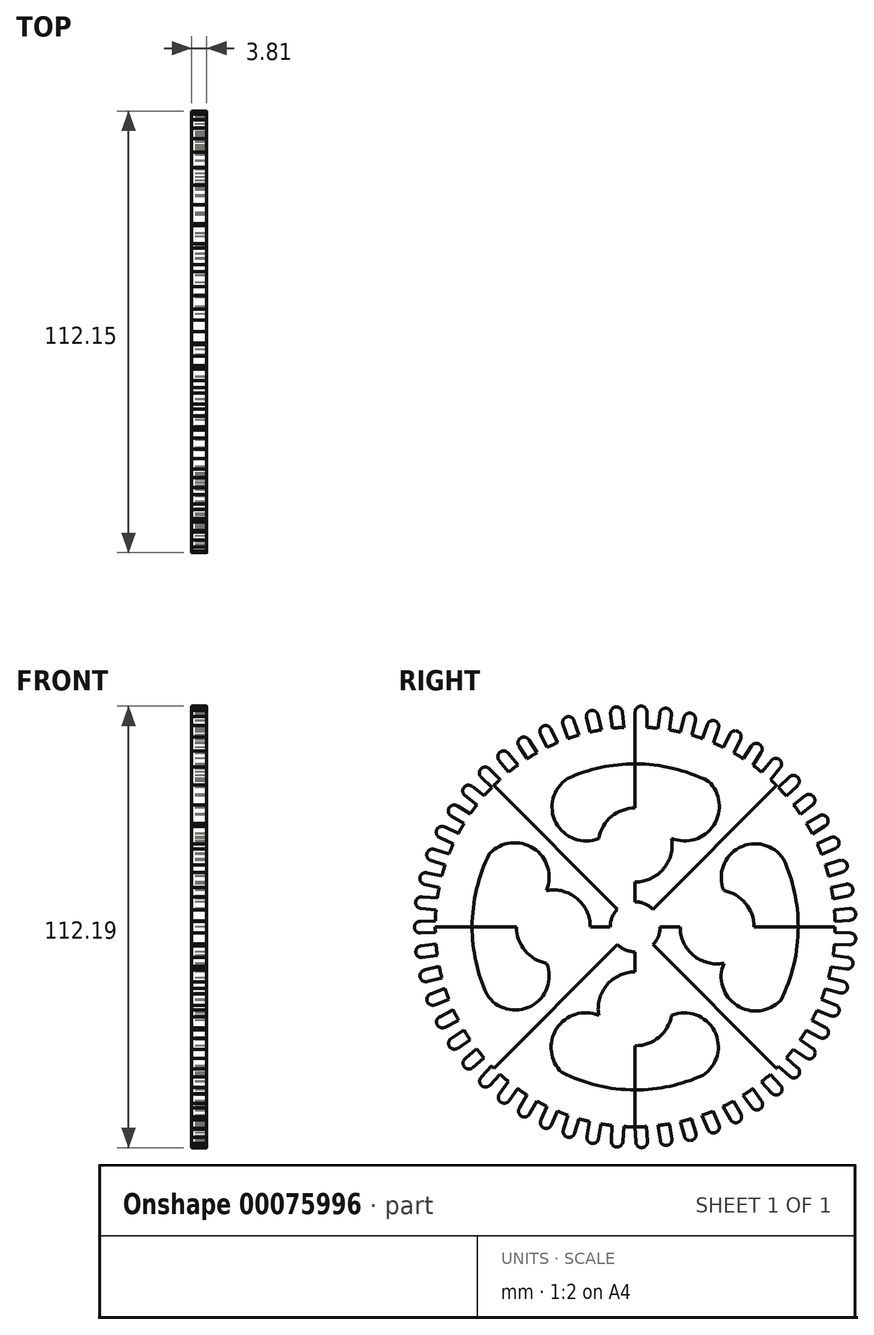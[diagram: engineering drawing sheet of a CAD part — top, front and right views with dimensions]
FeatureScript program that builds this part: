
annotation { "Feature Type Name" : "Feature", "Feature Type Description" : "" }
export const myFeature = defineFeature(function(context is Context, id is Id, definition is map)
    precondition{}
    {
        {
            var Q0;
            Q0=qCreatedBy(makeId("Right.planeOp"),FACE);
            var sketch = newSketch(context, id + "F0", { "sketchPlane" : qUnion([Q0])});
            skCircle(sketch, "E0", {"center": v(-2.48, 1.96) * mm, "radius": 50.8 * mm});
            skCircle(sketch, "E1", {"center": v(-2.48, 1.96) * mm, "radius": 6.35 * mm});
            skLineSegment(sketch, "E2", {"start": v(-2.48, 1.96) * mm, "end": v(-2.48, -48.84) * mm});
            skLineSegment(sketch, "E3.1.0", {"start": v(-2.48, 1.96) * mm, "end": v(33.44, -33.96) * mm});
            skLineSegment(sketch, "E3.2.0", {"start": v(-2.48, 1.96) * mm, "end": v(48.32, 1.96) * mm});
            skLineSegment(sketch, "E3.3.0", {"start": v(-2.48, 1.96) * mm, "end": v(33.44, 37.88) * mm});
            skLineSegment(sketch, "E3.4.0", {"start": v(-2.48, 1.96) * mm, "end": v(-2.48, 52.76) * mm});
            skLineSegment(sketch, "E3.5.0", {"start": v(-2.48, 1.96) * mm, "end": v(-38.4, 37.88) * mm});
            skLineSegment(sketch, "E3.6.0", {"start": v(-2.48, 1.96) * mm, "end": v(-53.28, 1.96) * mm});
            skLineSegment(sketch, "E3.7.0", {"start": v(-2.48, 1.96) * mm, "end": v(-38.4, -33.96) * mm});
            skCircle(sketch, "E4", {"center": v(-23.3, 1.96) * mm, "radius": 9.4 * mm});
            skCircle(sketch, "E5.1.0", {"center": v(-2.48, -18.85) * mm, "radius": 9.4 * mm});
            skCircle(sketch, "E5.2.0", {"center": v(18.34, 1.96) * mm, "radius": 9.4 * mm});
            skCircle(sketch, "E5.3.0", {"center": v(-2.48, 22.78) * mm, "radius": 9.4 * mm});
            skPoint(sketch, "E6", {"position": v(-11.72, 24.46) * mm});
            skPoint(sketch, "E7", {"position": v(6.76, 24.46) * mm});
            skPoint(sketch, "E8", {"position": v(20.02, 11.2) * mm});
            skPoint(sketch, "E9", {"position": v(20.02, -7.28) * mm});
            skPoint(sketch, "E10", {"position": v(6.76, -20.54) * mm});
            skPoint(sketch, "E11", {"position": v(-11.72, -20.54) * mm});
            skPoint(sketch, "E12", {"position": v(-24.97, -7.28) * mm});
            skPoint(sketch, "E13", {"position": v(-24.97, 11.2) * mm});
            skArc(sketch, "E14", {"start": v(-24.97, 11.2) * mm, "mid": v(-26.8, 1.96) * mm, "end": v(-24.97, -7.28) * mm});
            skArc(sketch, "E15.1.0", {"start": v(-11.72, -20.53) * mm, "mid": v(-2.48, -22.36) * mm, "end": v(6.77, -20.53) * mm});
            skArc(sketch, "E15.2.0", {"start": v(20.02, -7.28) * mm, "mid": v(21.84, 1.96) * mm, "end": v(20.02, 11.2) * mm});
            skArc(sketch, "E15.3.0", {"start": v(6.77, 24.45) * mm, "mid": v(-2.48, 26.28) * mm, "end": v(-11.72, 24.45) * mm});
            skArc(sketch, "E16", {"start": v(-11.72, -20.53) * mm, "mid": v(-22.43, -23.88) * mm, "end": v(-21.12, -35.03) * mm});
            skArc(sketch, "E17.1.0", {"start": v(20.02, -7.28) * mm, "mid": v(23.36, -18) * mm, "end": v(34.51, -16.68) * mm});
            skArc(sketch, "E17.2.0", {"start": v(6.77, 24.45) * mm, "mid": v(17.48, 27.8) * mm, "end": v(16.17, 38.95) * mm});
            skArc(sketch, "E17.3.0", {"start": v(-24.97, 11.2) * mm, "mid": v(-28.32, 21.92) * mm, "end": v(-39.47, 20.6) * mm});
            skArc(sketch, "E18", {"start": v(6.77, -20.53) * mm, "mid": v(17.66, -24.5) * mm, "end": v(14.73, -35.72) * mm});
            skArc(sketch, "E19.1.0", {"start": v(20.02, 11.2) * mm, "mid": v(23.98, 22.1) * mm, "end": v(35.2, 19.16) * mm});
            skArc(sketch, "E19.2.0", {"start": v(-11.72, 24.45) * mm, "mid": v(-22.62, 28.42) * mm, "end": v(-19.68, 39.64) * mm});
            skArc(sketch, "E19.3.0", {"start": v(-24.97, -7.28) * mm, "mid": v(-28.94, -18.18) * mm, "end": v(-40.16, -15.24) * mm});
            skArc(sketch, "E20", {"start": v(14.73, -35.72) * mm, "mid": v(-3.28, -39.45) * mm, "end": v(-21.12, -35.03) * mm});
            skArc(sketch, "E21.1.0", {"start": v(35.2, 19.16) * mm, "mid": v(38.94, 1.16) * mm, "end": v(34.51, -16.68) * mm});
            skArc(sketch, "E21.2.0", {"start": v(-19.68, 39.64) * mm, "mid": v(-1.68, 43.38) * mm, "end": v(16.17, 38.95) * mm});
            skArc(sketch, "E21.3.0", {"start": v(-40.16, -15.24) * mm, "mid": v(-43.9, 2.76) * mm, "end": v(-39.47, 20.6) * mm});
            skLineSegment(sketch, "E22", {"start": v(-2.48, 52.76) * mm, "end": v(-2.48, 56.57) * mm});
            skLineSegment(sketch, "E23", {"start": v(0.5, 52.67) * mm, "end": v(0.5, 56.48) * mm});
            skArc(sketch, "E24", {"start": v(0.5, 56.48) * mm, "mid": v(-0.95, 58.06) * mm, "end": v(-2.48, 56.57) * mm});
            skLineSegment(sketch, "E25.1.0", {"start": v(-8.27, 52.43) * mm, "end": v(-8.7, 56.21) * mm});
            skArc(sketch, "E25.1.1", {"start": v(-5.74, 56.47) * mm, "mid": v(-7.35, 57.87) * mm, "end": v(-8.7, 56.21) * mm});
            skLineSegment(sketch, "E25.1.2", {"start": v(-5.3, 52.68) * mm, "end": v(-5.74, 56.47) * mm});
            skLineSegment(sketch, "E25.2.0", {"start": v(-13.98, 51.44) * mm, "end": v(-14.85, 55.15) * mm});
            skArc(sketch, "E25.2.1", {"start": v(-11.93, 55.74) * mm, "mid": v(-13.7, 56.95) * mm, "end": v(-14.85, 55.15) * mm});
            skLineSegment(sketch, "E25.2.2", {"start": v(-11.07, 52.03) * mm, "end": v(-11.93, 55.74) * mm});
            skLineSegment(sketch, "E25.3.0", {"start": v(-19.55, 49.8) * mm, "end": v(-20.83, 53.4) * mm});
            skArc(sketch, "E25.3.1", {"start": v(-18, 54.31) * mm, "mid": v(-19.89, 55.3) * mm, "end": v(-20.83, 53.4) * mm});
            skLineSegment(sketch, "E25.3.2", {"start": v(-16.72, 50.72) * mm, "end": v(-18, 54.31) * mm});
            skLineSegment(sketch, "E25.4.0", {"start": v(-24.9, 47.55) * mm, "end": v(-26.57, 50.97) * mm});
            skArc(sketch, "E25.4.1", {"start": v(-23.87, 52.2) * mm, "mid": v(-25.85, 52.98) * mm, "end": v(-26.57, 50.97) * mm});
            skLineSegment(sketch, "E25.4.2", {"start": v(-22.19, 48.78) * mm, "end": v(-23.87, 52.2) * mm});
            skLineSegment(sketch, "E25.5.0", {"start": v(-29.94, 44.7) * mm, "end": v(-32, 47.9) * mm});
            skArc(sketch, "E25.5.1", {"start": v(-29.45, 49.44) * mm, "mid": v(-31.52, 49.98) * mm, "end": v(-32, 47.9) * mm});
            skLineSegment(sketch, "E25.5.2", {"start": v(-27.4, 46.23) * mm, "end": v(-29.45, 49.44) * mm});
            skLineSegment(sketch, "E25.6.0", {"start": v(-34.63, 41.29) * mm, "end": v(-37.05, 44.24) * mm});
            skArc(sketch, "E25.6.1", {"start": v(-34.7, 46.05) * mm, "mid": v(-36.8, 46.36) * mm, "end": v(-37.05, 44.24) * mm});
            skLineSegment(sketch, "E25.6.2", {"start": v(-32.28, 43.1) * mm, "end": v(-34.7, 46.05) * mm});
            skLineSegment(sketch, "E25.7.0", {"start": v(-38.9, 37.37) * mm, "end": v(-41.64, 40.02) * mm});
            skArc(sketch, "E25.7.1", {"start": v(-39.5, 42.1) * mm, "mid": v(-41.64, 42.15) * mm, "end": v(-41.64, 40.02) * mm});
            skLineSegment(sketch, "E25.7.2", {"start": v(-36.77, 39.44) * mm, "end": v(-39.5, 42.1) * mm});
            skLineSegment(sketch, "E25.8.0", {"start": v(-42.7, 32.98) * mm, "end": v(-45.72, 35.3) * mm});
            skArc(sketch, "E25.8.1", {"start": v(-43.84, 37.6) * mm, "mid": v(-45.97, 37.43) * mm, "end": v(-45.72, 35.3) * mm});
            skLineSegment(sketch, "E25.8.2", {"start": v(-40.82, 35.28) * mm, "end": v(-43.84, 37.6) * mm});
            skLineSegment(sketch, "E25.9.0", {"start": v(-45.98, 28.2) * mm, "end": v(-49.24, 30.16) * mm});
            skArc(sketch, "E25.9.1", {"start": v(-47.63, 32.66) * mm, "mid": v(-49.72, 32.24) * mm, "end": v(-49.24, 30.16) * mm});
            skLineSegment(sketch, "E25.9.2", {"start": v(-44.37, 30.7) * mm, "end": v(-47.63, 32.66) * mm});
            skLineSegment(sketch, "E25.10.0", {"start": v(-48.69, 23.06) * mm, "end": v(-52.15, 24.65) * mm});
            skArc(sketch, "E25.10.1", {"start": v(-50.84, 27.31) * mm, "mid": v(-52.87, 26.66) * mm, "end": v(-52.15, 24.65) * mm});
            skLineSegment(sketch, "E25.10.2", {"start": v(-47.37, 25.73) * mm, "end": v(-50.84, 27.31) * mm});
            skLineSegment(sketch, "E25.11.0", {"start": v(-50.8, 17.66) * mm, "end": v(-54.41, 18.84) * mm});
            skArc(sketch, "E25.11.1", {"start": v(-53.41, 21.64) * mm, "mid": v(-55.35, 20.75) * mm, "end": v(-54.41, 18.84) * mm});
            skLineSegment(sketch, "E25.11.2", {"start": v(-49.79, 20.46) * mm, "end": v(-53.41, 21.64) * mm});
            skLineSegment(sketch, "E25.12.0", {"start": v(-52.27, 12.05) * mm, "end": v(-56, 12.8) * mm});
            skArc(sketch, "E25.12.1", {"start": v(-55.32, 15.7) * mm, "mid": v(-57.15, 14.6) * mm, "end": v(-56, 12.8) * mm});
            skLineSegment(sketch, "E25.12.2", {"start": v(-51.59, 14.94) * mm, "end": v(-55.32, 15.7) * mm});
            skLineSegment(sketch, "E25.13.0", {"start": v(-53.1, 6.3) * mm, "end": v(-56.89, 6.63) * mm});
            skArc(sketch, "E25.13.1", {"start": v(-56.55, 9.59) * mm, "mid": v(-58.24, 8.29) * mm, "end": v(-56.89, 6.63) * mm});
            skLineSegment(sketch, "E25.13.2", {"start": v(-52.75, 9.26) * mm, "end": v(-56.55, 9.59) * mm});
            skLineSegment(sketch, "E25.14.0", {"start": v(-53.26, 0.51) * mm, "end": v(-57.06, 0.4) * mm});
            skArc(sketch, "E25.14.1", {"start": v(-57.06, 3.37) * mm, "mid": v(-58.6, 1.89) * mm, "end": v(-57.06, 0.4) * mm});
            skLineSegment(sketch, "E25.14.2", {"start": v(-53.25, 3.48) * mm, "end": v(-57.06, 3.37) * mm});
            skLineSegment(sketch, "E25.15.0", {"start": v(-52.76, -5.27) * mm, "end": v(-56.53, -5.81) * mm});
            skArc(sketch, "E25.15.1", {"start": v(-56.87, -2.86) * mm, "mid": v(-58.22, -4.5) * mm, "end": v(-56.53, -5.81) * mm});
            skLineSegment(sketch, "E25.15.2", {"start": v(-53.1, -2.31) * mm, "end": v(-56.87, -2.86) * mm});
            skLineSegment(sketch, "E25.16.0", {"start": v(-51.6, -10.95) * mm, "end": v(-55.3, -11.92) * mm});
            skArc(sketch, "E25.16.1", {"start": v(-55.96, -9.03) * mm, "mid": v(-57.12, -10.82) * mm, "end": v(-55.3, -11.92) * mm});
            skLineSegment(sketch, "E25.16.2", {"start": v(-52.28, -8.06) * mm, "end": v(-55.96, -9.03) * mm});
            skLineSegment(sketch, "E25.17.0", {"start": v(-49.82, -16.47) * mm, "end": v(-53.37, -17.85) * mm});
            skArc(sketch, "E25.17.1", {"start": v(-54.36, -15.05) * mm, "mid": v(-55.3, -16.96) * mm, "end": v(-53.37, -17.85) * mm});
            skLineSegment(sketch, "E25.17.2", {"start": v(-50.81, -13.67) * mm, "end": v(-54.36, -15.05) * mm});
            skLineSegment(sketch, "E25.18.0", {"start": v(-47.4, -21.75) * mm, "end": v(-50.78, -23.52) * mm});
            skArc(sketch, "E25.18.1", {"start": v(-52.09, -20.85) * mm, "mid": v(-52.8, -22.86) * mm, "end": v(-50.78, -23.52) * mm});
            skLineSegment(sketch, "E25.18.2", {"start": v(-48.72, -19.08) * mm, "end": v(-52.09, -20.85) * mm});
            skLineSegment(sketch, "E25.19.0", {"start": v(-44.41, -26.71) * mm, "end": v(-47.56, -28.86) * mm});
            skArc(sketch, "E25.19.1", {"start": v(-49.16, -26.36) * mm, "mid": v(-49.65, -28.44) * mm, "end": v(-47.56, -28.86) * mm});
            skLineSegment(sketch, "E25.19.2", {"start": v(-46.02, -24.21) * mm, "end": v(-49.16, -26.36) * mm});
            skLineSegment(sketch, "E25.20.0", {"start": v(-40.87, -31.3) * mm, "end": v(-43.75, -33.8) * mm});
            skArc(sketch, "E25.20.1", {"start": v(-45.63, -31.5) * mm, "mid": v(-45.87, -33.62) * mm, "end": v(-43.75, -33.8) * mm});
            skLineSegment(sketch, "E25.20.2", {"start": v(-42.75, -29) * mm, "end": v(-45.63, -31.5) * mm});
            skLineSegment(sketch, "E25.21.0", {"start": v(-36.83, -35.47) * mm, "end": v(-39.4, -38.27) * mm});
            skArc(sketch, "E25.21.1", {"start": v(-41.53, -36.2) * mm, "mid": v(-41.54, -38.33) * mm, "end": v(-39.4, -38.27) * mm});
            skLineSegment(sketch, "E25.21.2", {"start": v(-38.96, -33.4) * mm, "end": v(-41.53, -36.2) * mm});
            skLineSegment(sketch, "E25.22.0", {"start": v(-32.34, -39.14) * mm, "end": v(-34.58, -42.22) * mm});
            skArc(sketch, "E25.22.1", {"start": v(-36.93, -40.4) * mm, "mid": v(-36.69, -42.52) * mm, "end": v(-34.58, -42.22) * mm});
            skLineSegment(sketch, "E25.22.2", {"start": v(-34.69, -37.32) * mm, "end": v(-36.93, -40.4) * mm});
            skLineSegment(sketch, "E25.23.0", {"start": v(-27.46, -42.27) * mm, "end": v(-29.33, -45.6) * mm});
            skArc(sketch, "E25.23.1", {"start": v(-31.88, -44.05) * mm, "mid": v(-31.4, -46.13) * mm, "end": v(-29.33, -45.6) * mm});
            skLineSegment(sketch, "E25.23.2", {"start": v(-30, -40.74) * mm, "end": v(-31.88, -44.05) * mm});
            skLineSegment(sketch, "E25.24.0", {"start": v(-22.25, -44.83) * mm, "end": v(-23.74, -48.34) * mm});
            skArc(sketch, "E25.24.1", {"start": v(-26.44, -47.1) * mm, "mid": v(-25.72, -49.12) * mm, "end": v(-23.74, -48.34) * mm});
            skLineSegment(sketch, "E25.24.2", {"start": v(-24.96, -43.6) * mm, "end": v(-26.44, -47.1) * mm});
            skLineSegment(sketch, "E25.25.0", {"start": v(-16.79, -46.78) * mm, "end": v(-17.86, -50.44) * mm});
            skArc(sketch, "E25.25.1", {"start": v(-20.69, -49.52) * mm, "mid": v(-19.75, -51.43) * mm, "end": v(-17.86, -50.44) * mm});
            skLineSegment(sketch, "E25.25.2", {"start": v(-19.62, -45.86) * mm, "end": v(-20.69, -49.52) * mm});
            skLineSegment(sketch, "E25.26.0", {"start": v(-11.14, -48.1) * mm, "end": v(-11.79, -51.85) * mm});
            skArc(sketch, "E25.26.1", {"start": v(-14.7, -51.26) * mm, "mid": v(-13.55, -53.05) * mm, "end": v(-11.79, -51.85) * mm});
            skLineSegment(sketch, "E25.26.2", {"start": v(-14.05, -47.5) * mm, "end": v(-14.7, -51.26) * mm});
            skLineSegment(sketch, "E25.27.0", {"start": v(-5.38, -48.76) * mm, "end": v(-5.6, -52.56) * mm});
            skArc(sketch, "E25.27.1", {"start": v(-8.56, -52.3) * mm, "mid": v(-7.2, -53.96) * mm, "end": v(-5.6, -52.56) * mm});
            skLineSegment(sketch, "E25.27.2", {"start": v(-8.34, -48.5) * mm, "end": v(-8.56, -52.3) * mm});
            skLineSegment(sketch, "E25.28.0", {"start": v(0.42, -48.76) * mm, "end": v(0.64, -52.56) * mm});
            skArc(sketch, "E25.28.1", {"start": v(-2.33, -52.64) * mm, "mid": v(-0.8, -54.13) * mm, "end": v(0.64, -52.56) * mm});
            skLineSegment(sketch, "E25.28.2", {"start": v(-2.55, -48.84) * mm, "end": v(-2.33, -52.64) * mm});
            skLineSegment(sketch, "E25.29.0", {"start": v(6.19, -48.1) * mm, "end": v(6.84, -51.85) * mm});
            skArc(sketch, "E25.29.1", {"start": v(3.9, -52.27) * mm, "mid": v(5.58, -53.57) * mm, "end": v(6.84, -51.85) * mm});
            skLineSegment(sketch, "E25.29.2", {"start": v(3.24, -48.52) * mm, "end": v(3.9, -52.27) * mm});
            skLineSegment(sketch, "E25.30.0", {"start": v(11.84, -46.78) * mm, "end": v(12.9, -50.44) * mm});
            skArc(sketch, "E25.30.1", {"start": v(10.03, -51.2) * mm, "mid": v(11.86, -52.3) * mm, "end": v(12.9, -50.44) * mm});
            skLineSegment(sketch, "E25.30.2", {"start": v(8.96, -47.54) * mm, "end": v(10.03, -51.2) * mm});
            skLineSegment(sketch, "E25.31.0", {"start": v(17.3, -44.83) * mm, "end": v(18.78, -48.34) * mm});
            skArc(sketch, "E25.31.1", {"start": v(16, -49.42) * mm, "mid": v(17.95, -50.3) * mm, "end": v(18.78, -48.34) * mm});
            skLineSegment(sketch, "E25.31.2", {"start": v(14.53, -45.9) * mm, "end": v(16, -49.42) * mm});
            skLineSegment(sketch, "E25.32.0", {"start": v(22.5, -42.27) * mm, "end": v(24.38, -45.6) * mm});
            skArc(sketch, "E25.32.1", {"start": v(21.75, -46.98) * mm, "mid": v(23.77, -47.64) * mm, "end": v(24.38, -45.6) * mm});
            skLineSegment(sketch, "E25.32.2", {"start": v(19.87, -43.66) * mm, "end": v(21.75, -46.98) * mm});
            skLineSegment(sketch, "E25.33.0", {"start": v(27.38, -39.14) * mm, "end": v(29.62, -42.22) * mm});
            skArc(sketch, "E25.33.1", {"start": v(27.17, -43.9) * mm, "mid": v(29.26, -44.32) * mm, "end": v(29.62, -42.22) * mm});
            skLineSegment(sketch, "E25.33.2", {"start": v(24.93, -40.81) * mm, "end": v(27.17, -43.9) * mm});
            skLineSegment(sketch, "E25.34.0", {"start": v(31.87, -35.47) * mm, "end": v(34.45, -38.27) * mm});
            skArc(sketch, "E25.34.1", {"start": v(32.2, -40.22) * mm, "mid": v(34.33, -40.4) * mm, "end": v(34.45, -38.27) * mm});
            skLineSegment(sketch, "E25.34.2", {"start": v(29.62, -37.41) * mm, "end": v(32.2, -40.22) * mm});
            skLineSegment(sketch, "E25.35.0", {"start": v(35.92, -31.3) * mm, "end": v(38.8, -33.8) * mm});
            skArc(sketch, "E25.35.1", {"start": v(36.78, -35.99) * mm, "mid": v(38.92, -35.93) * mm, "end": v(38.8, -33.8) * mm});
            skLineSegment(sketch, "E25.35.2", {"start": v(33.9, -33.5) * mm, "end": v(36.78, -35.99) * mm});
            skLineSegment(sketch, "E25.36.0", {"start": v(39.46, -26.71) * mm, "end": v(42.6, -28.86) * mm});
            skArc(sketch, "E25.36.1", {"start": v(40.85, -31.27) * mm, "mid": v(42.97, -30.97) * mm, "end": v(42.6, -28.86) * mm});
            skLineSegment(sketch, "E25.36.2", {"start": v(37.7, -29.12) * mm, "end": v(40.85, -31.27) * mm});
            skLineSegment(sketch, "E25.37.0", {"start": v(42.45, -21.75) * mm, "end": v(45.82, -23.52) * mm});
            skArc(sketch, "E25.37.1", {"start": v(44.36, -26.11) * mm, "mid": v(46.42, -25.57) * mm, "end": v(45.82, -23.52) * mm});
            skLineSegment(sketch, "E25.37.2", {"start": v(40.99, -24.33) * mm, "end": v(44.36, -26.11) * mm});
            skLineSegment(sketch, "E25.38.0", {"start": v(44.86, -16.47) * mm, "end": v(48.41, -17.85) * mm});
            skArc(sketch, "E25.38.1", {"start": v(47.25, -20.59) * mm, "mid": v(49.24, -19.82) * mm, "end": v(48.41, -17.85) * mm});
            skLineSegment(sketch, "E25.38.2", {"start": v(43.7, -19.2) * mm, "end": v(47.25, -20.59) * mm});
            skLineSegment(sketch, "E25.39.0", {"start": v(46.65, -10.95) * mm, "end": v(50.34, -11.92) * mm});
            skArc(sketch, "E25.39.1", {"start": v(49.5, -14.77) * mm, "mid": v(51.39, -13.78) * mm, "end": v(50.34, -11.92) * mm});
            skLineSegment(sketch, "E25.39.2", {"start": v(45.81, -13.8) * mm, "end": v(49.5, -14.77) * mm});
            skLineSegment(sketch, "E25.40.0", {"start": v(47.8, -5.27) * mm, "end": v(51.58, -5.81) * mm});
            skArc(sketch, "E25.40.1", {"start": v(51.07, -8.74) * mm, "mid": v(52.83, -7.54) * mm, "end": v(51.58, -5.81) * mm});
            skLineSegment(sketch, "E25.40.2", {"start": v(47.3, -8.2) * mm, "end": v(51.07, -8.74) * mm});
            skLineSegment(sketch, "E25.41.0", {"start": v(48.3, 0.51) * mm, "end": v(52.11, 0.4) * mm});
            skArc(sketch, "E25.41.1", {"start": v(51.94, -2.57) * mm, "mid": v(53.55, -1.17) * mm, "end": v(52.11, 0.4) * mm});
            skLineSegment(sketch, "E25.41.2", {"start": v(48.13, -2.46) * mm, "end": v(51.94, -2.57) * mm});
            skLineSegment(sketch, "E25.42.0", {"start": v(48.14, 6.3) * mm, "end": v(51.93, 6.63) * mm});
            skArc(sketch, "E25.42.1", {"start": v(52.1, 3.67) * mm, "mid": v(53.54, 5.24) * mm, "end": v(51.93, 6.63) * mm});
            skLineSegment(sketch, "E25.42.2", {"start": v(48.3, 3.34) * mm, "end": v(52.1, 3.67) * mm});
            skLineSegment(sketch, "E25.43.0", {"start": v(47.31, 12.05) * mm, "end": v(51.05, 12.8) * mm});
            skArc(sketch, "E25.43.1", {"start": v(51.55, 9.88) * mm, "mid": v(52.8, 11.6) * mm, "end": v(51.05, 12.8) * mm});
            skLineSegment(sketch, "E25.43.2", {"start": v(47.82, 9.12) * mm, "end": v(51.55, 9.88) * mm});
            skLineSegment(sketch, "E25.44.0", {"start": v(45.84, 17.66) * mm, "end": v(49.46, 18.84) * mm});
            skArc(sketch, "E25.44.1", {"start": v(50.3, 15.98) * mm, "mid": v(51.35, 17.84) * mm, "end": v(49.46, 18.84) * mm});
            skLineSegment(sketch, "E25.44.2", {"start": v(46.67, 14.8) * mm, "end": v(50.3, 15.98) * mm});
            skLineSegment(sketch, "E25.45.0", {"start": v(43.73, 23.06) * mm, "end": v(47.2, 24.65) * mm});
            skArc(sketch, "E25.45.1", {"start": v(48.35, 21.9) * mm, "mid": v(49.19, 23.87) * mm, "end": v(47.2, 24.65) * mm});
            skLineSegment(sketch, "E25.45.2", {"start": v(44.89, 20.32) * mm, "end": v(48.35, 21.9) * mm});
            skLineSegment(sketch, "E25.46.0", {"start": v(41.03, 28.2) * mm, "end": v(44.29, 30.16) * mm});
            skArc(sketch, "E25.46.1", {"start": v(45.75, 27.57) * mm, "mid": v(46.35, 29.62) * mm, "end": v(44.29, 30.16) * mm});
            skLineSegment(sketch, "E25.46.2", {"start": v(42.49, 25.6) * mm, "end": v(45.75, 27.57) * mm});
            skLineSegment(sketch, "E25.47.0", {"start": v(37.75, 32.98) * mm, "end": v(40.77, 35.3) * mm});
            skArc(sketch, "E25.47.1", {"start": v(42.51, 32.9) * mm, "mid": v(42.88, 35) * mm, "end": v(40.77, 35.3) * mm});
            skLineSegment(sketch, "E25.47.2", {"start": v(39.5, 30.58) * mm, "end": v(42.51, 32.9) * mm});
            skLineSegment(sketch, "E25.48.0", {"start": v(33.95, 37.37) * mm, "end": v(36.69, 40.02) * mm});
            skArc(sketch, "E25.48.1", {"start": v(38.7, 37.83) * mm, "mid": v(38.82, 39.96) * mm, "end": v(36.69, 40.02) * mm});
            skLineSegment(sketch, "E25.48.2", {"start": v(35.96, 35.17) * mm, "end": v(38.7, 37.83) * mm});
            skLineSegment(sketch, "E25.49.0", {"start": v(29.68, 41.29) * mm, "end": v(32.1, 44.24) * mm});
            skArc(sketch, "E25.49.1", {"start": v(34.34, 42.29) * mm, "mid": v(34.22, 44.42) * mm, "end": v(32.1, 44.24) * mm});
            skLineSegment(sketch, "E25.49.2", {"start": v(31.93, 39.34) * mm, "end": v(34.34, 42.29) * mm});
            skLineSegment(sketch, "E25.50.0", {"start": v(24.99, 44.7) * mm, "end": v(27.05, 47.9) * mm});
            skArc(sketch, "E25.50.1", {"start": v(29.5, 46.22) * mm, "mid": v(29.14, 48.32) * mm, "end": v(27.05, 47.9) * mm});
            skLineSegment(sketch, "E25.50.2", {"start": v(27.44, 43.02) * mm, "end": v(29.5, 46.22) * mm});
            skLineSegment(sketch, "E25.51.0", {"start": v(19.94, 47.55) * mm, "end": v(21.62, 50.97) * mm});
            skArc(sketch, "E25.51.1", {"start": v(24.25, 49.58) * mm, "mid": v(23.65, 51.63) * mm, "end": v(21.62, 50.97) * mm});
            skLineSegment(sketch, "E25.51.2", {"start": v(22.57, 46.16) * mm, "end": v(24.25, 49.58) * mm});
            skLineSegment(sketch, "E25.52.0", {"start": v(14.6, 49.8) * mm, "end": v(15.87, 53.4) * mm});
            skArc(sketch, "E25.52.1", {"start": v(18.64, 52.31) * mm, "mid": v(17.82, 54.28) * mm, "end": v(15.87, 53.4) * mm});
            skLineSegment(sketch, "E25.52.2", {"start": v(17.36, 48.73) * mm, "end": v(18.64, 52.31) * mm});
            skLineSegment(sketch, "E25.53.0", {"start": v(9.03, 51.44) * mm, "end": v(9.9, 55.15) * mm});
            skArc(sketch, "E25.53.1", {"start": v(12.77, 54.4) * mm, "mid": v(11.72, 56.25) * mm, "end": v(9.9, 55.15) * mm});
            skLineSegment(sketch, "E25.53.2", {"start": v(11.9, 50.68) * mm, "end": v(12.77, 54.4) * mm});
            skLineSegment(sketch, "E25.54.0", {"start": v(3.31, 52.43) * mm, "end": v(3.75, 56.21) * mm});
            skArc(sketch, "E25.54.1", {"start": v(6.7, 55.79) * mm, "mid": v(5.44, 57.52) * mm, "end": v(3.75, 56.21) * mm});
            skLineSegment(sketch, "E25.54.2", {"start": v(6.26, 52) * mm, "end": v(6.7, 55.79) * mm});
            skSolve(sketch);
        }
        {
            var Q0;
            {var subQ12=sQuery(id+"F0.wireOp",EDGE,"E17.2.0");Q0=makeQuery(id+"F0.imprint","IMPRINT",FACE,{"disambiguationData":[TD([[makeQuery(id+"F0.imprint","IMPRINT",EDGE,{"derivedFrom":subQ12}),-1.0]])]});}
            var Q1;
            {var subQ17=sQuery(id+"F0.wireOp",EDGE,"E19.1.0");Q1=makeQuery(id+"F0.imprint","IMPRINT",FACE,{"disambiguationData":[TD([[makeQuery(id+"F0.imprint","IMPRINT",EDGE,{"derivedFrom":subQ17}),1.0]])]});}
            var Q2;
            {var subQ12=sQuery(id+"F0.wireOp",EDGE,"E17.1.0");Q2=makeQuery(id+"F0.imprint","IMPRINT",FACE,{"disambiguationData":[TD([[makeQuery(id+"F0.imprint","IMPRINT",EDGE,{"derivedFrom":subQ12}),-1.0]])]});}
            var Q3;
            {var subQ16=sQuery(id+"F0.wireOp",EDGE,"E18");Q3=makeQuery(id+"F0.imprint","IMPRINT",FACE,{"disambiguationData":[TD([[makeQuery(id+"F0.imprint","IMPRINT",EDGE,{"derivedFrom":subQ16}),1.0]])]});}
            var Q4;
            {var subQ22=sQuery(id+"F0.wireOp",EDGE,"E16");Q4=makeQuery(id+"F0.imprint","IMPRINT",FACE,{"disambiguationData":[TD([[makeQuery(id+"F0.imprint","IMPRINT",EDGE,{"derivedFrom":subQ22}),-1.0]])]});}
            var Q5;
            {var subQ10=sQuery(id+"F0.wireOp",EDGE,"E19.3.0");Q5=makeQuery(id+"F0.imprint","IMPRINT",FACE,{"disambiguationData":[TD([[makeQuery(id+"F0.imprint","IMPRINT",EDGE,{"derivedFrom":subQ10}),1.0]])]});}
            var Q6;
            {var subQ13=sQuery(id+"F0.wireOp",EDGE,"E17.3.0");Q6=makeQuery(id+"F0.imprint","IMPRINT",FACE,{"disambiguationData":[TD([[makeQuery(id+"F0.imprint","IMPRINT",EDGE,{"derivedFrom":subQ13}),-1.0]])]});}
            var Q7;
            {var subQ13=sQuery(id+"F0.wireOp",EDGE,"E19.2.0");Q7=makeQuery(id+"F0.imprint","IMPRINT",FACE,{"disambiguationData":[TD([[makeQuery(id+"F0.imprint","IMPRINT",EDGE,{"derivedFrom":subQ13}),1.0]])]});}
            var Q8;
            {var subQ0=sQuery(id+"F0.wireOp",EDGE,"E25.8.0");Q8=makeQuery(id+"F0.imprint","IMPRINT",FACE,{"disambiguationData":[TD([[makeQuery(id+"F0.imprint","IMPRINT",EDGE,{"derivedFrom":subQ0}),-1.0]])]});}
            var Q9;
            {var subQ0=sQuery(id+"F0.wireOp",EDGE,"E25.9.0");Q9=makeQuery(id+"F0.imprint","IMPRINT",FACE,{"disambiguationData":[TD([[makeQuery(id+"F0.imprint","IMPRINT",EDGE,{"derivedFrom":subQ0}),-1.0]])]});}
            var Q10;
            {var subQ0=sQuery(id+"F0.wireOp",EDGE,"E25.10.0");Q10=makeQuery(id+"F0.imprint","IMPRINT",FACE,{"disambiguationData":[TD([[makeQuery(id+"F0.imprint","IMPRINT",EDGE,{"derivedFrom":subQ0}),-1.0]])]});}
            var Q11;
            {var subQ0=sQuery(id+"F0.wireOp",EDGE,"E25.11.0");Q11=makeQuery(id+"F0.imprint","IMPRINT",FACE,{"disambiguationData":[TD([[makeQuery(id+"F0.imprint","IMPRINT",EDGE,{"derivedFrom":subQ0}),-1.0]])]});}
            var Q12;
            {var subQ0=sQuery(id+"F0.wireOp",EDGE,"E25.12.0");Q12=makeQuery(id+"F0.imprint","IMPRINT",FACE,{"disambiguationData":[TD([[makeQuery(id+"F0.imprint","IMPRINT",EDGE,{"derivedFrom":subQ0}),-1.0]])]});}
            var Q13;
            {var subQ0=sQuery(id+"F0.wireOp",EDGE,"E25.13.0");Q13=makeQuery(id+"F0.imprint","IMPRINT",FACE,{"disambiguationData":[TD([[makeQuery(id+"F0.imprint","IMPRINT",EDGE,{"derivedFrom":subQ0}),-1.0]])]});}
            var Q14;
            {var subQ0=sQuery(id+"F0.wireOp",EDGE,"E25.14.0");Q14=makeQuery(id+"F0.imprint","IMPRINT",FACE,{"disambiguationData":[TD([[makeQuery(id+"F0.imprint","IMPRINT",EDGE,{"derivedFrom":subQ0}),-1.0]])]});}
            var Q15;
            {var subQ0=sQuery(id+"F0.wireOp",EDGE,"E25.15.0");Q15=makeQuery(id+"F0.imprint","IMPRINT",FACE,{"disambiguationData":[TD([[makeQuery(id+"F0.imprint","IMPRINT",EDGE,{"derivedFrom":subQ0}),-1.0]])]});}
            var Q16;
            {var subQ0=sQuery(id+"F0.wireOp",EDGE,"E25.16.0");Q16=makeQuery(id+"F0.imprint","IMPRINT",FACE,{"disambiguationData":[TD([[makeQuery(id+"F0.imprint","IMPRINT",EDGE,{"derivedFrom":subQ0}),-1.0]])]});}
            var Q17;
            {var subQ0=sQuery(id+"F0.wireOp",EDGE,"E25.17.0");Q17=makeQuery(id+"F0.imprint","IMPRINT",FACE,{"disambiguationData":[TD([[makeQuery(id+"F0.imprint","IMPRINT",EDGE,{"derivedFrom":subQ0}),-1.0]])]});}
            var Q18;
            {var subQ0=sQuery(id+"F0.wireOp",EDGE,"E25.18.0");Q18=makeQuery(id+"F0.imprint","IMPRINT",FACE,{"disambiguationData":[TD([[makeQuery(id+"F0.imprint","IMPRINT",EDGE,{"derivedFrom":subQ0}),-1.0]])]});}
            var Q19;
            {var subQ0=sQuery(id+"F0.wireOp",EDGE,"E25.19.0");Q19=makeQuery(id+"F0.imprint","IMPRINT",FACE,{"disambiguationData":[TD([[makeQuery(id+"F0.imprint","IMPRINT",EDGE,{"derivedFrom":subQ0}),-1.0]])]});}
            var Q20;
            {var subQ0=sQuery(id+"F0.wireOp",EDGE,"E25.20.0");Q20=makeQuery(id+"F0.imprint","IMPRINT",FACE,{"disambiguationData":[TD([[makeQuery(id+"F0.imprint","IMPRINT",EDGE,{"derivedFrom":subQ0}),-1.0]])]});}
            var Q21;
            {var subQ0=sQuery(id+"F0.wireOp",EDGE,"E25.21.0");Q21=makeQuery(id+"F0.imprint","IMPRINT",FACE,{"disambiguationData":[TD([[makeQuery(id+"F0.imprint","IMPRINT",EDGE,{"derivedFrom":subQ0}),-1.0]])]});}
            var Q22;
            {var subQ0=sQuery(id+"F0.wireOp",EDGE,"E25.22.0");Q22=makeQuery(id+"F0.imprint","IMPRINT",FACE,{"disambiguationData":[TD([[makeQuery(id+"F0.imprint","IMPRINT",EDGE,{"derivedFrom":subQ0}),-1.0]])]});}
            var Q23;
            {var subQ0=sQuery(id+"F0.wireOp",EDGE,"E25.23.0");Q23=makeQuery(id+"F0.imprint","IMPRINT",FACE,{"disambiguationData":[TD([[makeQuery(id+"F0.imprint","IMPRINT",EDGE,{"derivedFrom":subQ0}),-1.0]])]});}
            var Q24;
            {var subQ0=sQuery(id+"F0.wireOp",EDGE,"E25.24.0");Q24=makeQuery(id+"F0.imprint","IMPRINT",FACE,{"disambiguationData":[TD([[makeQuery(id+"F0.imprint","IMPRINT",EDGE,{"derivedFrom":subQ0}),-1.0]])]});}
            var Q25;
            {var subQ0=sQuery(id+"F0.wireOp",EDGE,"E25.25.0");Q25=makeQuery(id+"F0.imprint","IMPRINT",FACE,{"disambiguationData":[TD([[makeQuery(id+"F0.imprint","IMPRINT",EDGE,{"derivedFrom":subQ0}),-1.0]])]});}
            var Q26;
            {var subQ0=sQuery(id+"F0.wireOp",EDGE,"E25.26.0");Q26=makeQuery(id+"F0.imprint","IMPRINT",FACE,{"disambiguationData":[TD([[makeQuery(id+"F0.imprint","IMPRINT",EDGE,{"derivedFrom":subQ0}),-1.0]])]});}
            var Q27;
            {var subQ0=sQuery(id+"F0.wireOp",EDGE,"E25.27.0");Q27=makeQuery(id+"F0.imprint","IMPRINT",FACE,{"disambiguationData":[TD([[makeQuery(id+"F0.imprint","IMPRINT",EDGE,{"derivedFrom":subQ0}),-1.0]])]});}
            var Q28;
            {var subQ2=sQuery(id+"F0.wireOp",EDGE,"E25.28.0");Q28=makeQuery(id+"F0.imprint","IMPRINT",FACE,{"disambiguationData":[TD([[makeQuery(id+"F0.imprint","IMPRINT",EDGE,{"derivedFrom":subQ2}),-1.0]])]});}
            var Q29;
            {var subQ0=sQuery(id+"F0.wireOp",EDGE,"E25.29.0");Q29=makeQuery(id+"F0.imprint","IMPRINT",FACE,{"disambiguationData":[TD([[makeQuery(id+"F0.imprint","IMPRINT",EDGE,{"derivedFrom":subQ0}),-1.0]])]});}
            var Q30;
            {var subQ0=sQuery(id+"F0.wireOp",EDGE,"E25.30.0");Q30=makeQuery(id+"F0.imprint","IMPRINT",FACE,{"disambiguationData":[TD([[makeQuery(id+"F0.imprint","IMPRINT",EDGE,{"derivedFrom":subQ0}),-1.0]])]});}
            var Q31;
            {var subQ0=sQuery(id+"F0.wireOp",EDGE,"E25.31.0");Q31=makeQuery(id+"F0.imprint","IMPRINT",FACE,{"disambiguationData":[TD([[makeQuery(id+"F0.imprint","IMPRINT",EDGE,{"derivedFrom":subQ0}),-1.0]])]});}
            var Q32;
            {var subQ0=sQuery(id+"F0.wireOp",EDGE,"E25.32.0");Q32=makeQuery(id+"F0.imprint","IMPRINT",FACE,{"disambiguationData":[TD([[makeQuery(id+"F0.imprint","IMPRINT",EDGE,{"derivedFrom":subQ0}),-1.0]])]});}
            var Q33;
            {var subQ0=sQuery(id+"F0.wireOp",EDGE,"E25.33.0");Q33=makeQuery(id+"F0.imprint","IMPRINT",FACE,{"disambiguationData":[TD([[makeQuery(id+"F0.imprint","IMPRINT",EDGE,{"derivedFrom":subQ0}),-1.0]])]});}
            var Q34;
            {var subQ0=sQuery(id+"F0.wireOp",EDGE,"E25.34.0");Q34=makeQuery(id+"F0.imprint","IMPRINT",FACE,{"disambiguationData":[TD([[makeQuery(id+"F0.imprint","IMPRINT",EDGE,{"derivedFrom":subQ0}),-1.0]])]});}
            var Q35;
            {var subQ0=sQuery(id+"F0.wireOp",EDGE,"E25.35.0");Q35=makeQuery(id+"F0.imprint","IMPRINT",FACE,{"disambiguationData":[TD([[makeQuery(id+"F0.imprint","IMPRINT",EDGE,{"derivedFrom":subQ0}),-1.0]])]});}
            var Q36;
            {var subQ0=sQuery(id+"F0.wireOp",EDGE,"E25.36.0");Q36=makeQuery(id+"F0.imprint","IMPRINT",FACE,{"disambiguationData":[TD([[makeQuery(id+"F0.imprint","IMPRINT",EDGE,{"derivedFrom":subQ0}),-1.0]])]});}
            var Q37;
            {var subQ0=sQuery(id+"F0.wireOp",EDGE,"E25.37.0");Q37=makeQuery(id+"F0.imprint","IMPRINT",FACE,{"disambiguationData":[TD([[makeQuery(id+"F0.imprint","IMPRINT",EDGE,{"derivedFrom":subQ0}),-1.0]])]});}
            var Q38;
            {var subQ0=sQuery(id+"F0.wireOp",EDGE,"E25.38.0");Q38=makeQuery(id+"F0.imprint","IMPRINT",FACE,{"disambiguationData":[TD([[makeQuery(id+"F0.imprint","IMPRINT",EDGE,{"derivedFrom":subQ0}),-1.0]])]});}
            var Q39;
            {var subQ0=sQuery(id+"F0.wireOp",EDGE,"E25.39.0");Q39=makeQuery(id+"F0.imprint","IMPRINT",FACE,{"disambiguationData":[TD([[makeQuery(id+"F0.imprint","IMPRINT",EDGE,{"derivedFrom":subQ0}),-1.0]])]});}
            var Q40;
            {var subQ0=sQuery(id+"F0.wireOp",EDGE,"E25.40.0");Q40=makeQuery(id+"F0.imprint","IMPRINT",FACE,{"disambiguationData":[TD([[makeQuery(id+"F0.imprint","IMPRINT",EDGE,{"derivedFrom":subQ0}),-1.0]])]});}
            var Q41;
            {var subQ0=sQuery(id+"F0.wireOp",EDGE,"E25.41.0");Q41=makeQuery(id+"F0.imprint","IMPRINT",FACE,{"disambiguationData":[TD([[makeQuery(id+"F0.imprint","IMPRINT",EDGE,{"derivedFrom":subQ0}),-1.0]])]});}
            var Q42;
            {var subQ0=sQuery(id+"F0.wireOp",EDGE,"E25.42.0");Q42=makeQuery(id+"F0.imprint","IMPRINT",FACE,{"disambiguationData":[TD([[makeQuery(id+"F0.imprint","IMPRINT",EDGE,{"derivedFrom":subQ0}),-1.0]])]});}
            var Q43;
            {var subQ0=sQuery(id+"F0.wireOp",EDGE,"E25.43.0");Q43=makeQuery(id+"F0.imprint","IMPRINT",FACE,{"disambiguationData":[TD([[makeQuery(id+"F0.imprint","IMPRINT",EDGE,{"derivedFrom":subQ0}),-1.0]])]});}
            var Q44;
            {var subQ0=sQuery(id+"F0.wireOp",EDGE,"E25.44.0");Q44=makeQuery(id+"F0.imprint","IMPRINT",FACE,{"disambiguationData":[TD([[makeQuery(id+"F0.imprint","IMPRINT",EDGE,{"derivedFrom":subQ0}),-1.0]])]});}
            var Q45;
            {var subQ0=sQuery(id+"F0.wireOp",EDGE,"E25.45.0");Q45=makeQuery(id+"F0.imprint","IMPRINT",FACE,{"disambiguationData":[TD([[makeQuery(id+"F0.imprint","IMPRINT",EDGE,{"derivedFrom":subQ0}),-1.0]])]});}
            var Q46;
            {var subQ0=sQuery(id+"F0.wireOp",EDGE,"E25.46.0");Q46=makeQuery(id+"F0.imprint","IMPRINT",FACE,{"disambiguationData":[TD([[makeQuery(id+"F0.imprint","IMPRINT",EDGE,{"derivedFrom":subQ0}),-1.0]])]});}
            var Q47;
            {var subQ0=sQuery(id+"F0.wireOp",EDGE,"E25.47.0");Q47=makeQuery(id+"F0.imprint","IMPRINT",FACE,{"disambiguationData":[TD([[makeQuery(id+"F0.imprint","IMPRINT",EDGE,{"derivedFrom":subQ0}),-1.0]])]});}
            var Q48;
            {var subQ0=sQuery(id+"F0.wireOp",EDGE,"E25.48.0");Q48=makeQuery(id+"F0.imprint","IMPRINT",FACE,{"disambiguationData":[TD([[makeQuery(id+"F0.imprint","IMPRINT",EDGE,{"derivedFrom":subQ0}),-1.0]])]});}
            var Q49;
            {var subQ0=sQuery(id+"F0.wireOp",EDGE,"E25.49.0");Q49=makeQuery(id+"F0.imprint","IMPRINT",FACE,{"disambiguationData":[TD([[makeQuery(id+"F0.imprint","IMPRINT",EDGE,{"derivedFrom":subQ0}),-1.0]])]});}
            var Q50;
            {var subQ0=sQuery(id+"F0.wireOp",EDGE,"E25.50.0");Q50=makeQuery(id+"F0.imprint","IMPRINT",FACE,{"disambiguationData":[TD([[makeQuery(id+"F0.imprint","IMPRINT",EDGE,{"derivedFrom":subQ0}),-1.0]])]});}
            var Q51;
            {var subQ0=sQuery(id+"F0.wireOp",EDGE,"E25.51.0");Q51=makeQuery(id+"F0.imprint","IMPRINT",FACE,{"disambiguationData":[TD([[makeQuery(id+"F0.imprint","IMPRINT",EDGE,{"derivedFrom":subQ0}),-1.0]])]});}
            var Q52;
            {var subQ0=sQuery(id+"F0.wireOp",EDGE,"E25.52.0");Q52=makeQuery(id+"F0.imprint","IMPRINT",FACE,{"disambiguationData":[TD([[makeQuery(id+"F0.imprint","IMPRINT",EDGE,{"derivedFrom":subQ0}),-1.0]])]});}
            var Q53;
            {var subQ0=sQuery(id+"F0.wireOp",EDGE,"E25.53.0");Q53=makeQuery(id+"F0.imprint","IMPRINT",FACE,{"disambiguationData":[TD([[makeQuery(id+"F0.imprint","IMPRINT",EDGE,{"derivedFrom":subQ0}),-1.0]])]});}
            var Q54;
            {var subQ0=sQuery(id+"F0.wireOp",EDGE,"E25.54.0");Q54=makeQuery(id+"F0.imprint","IMPRINT",FACE,{"disambiguationData":[TD([[makeQuery(id+"F0.imprint","IMPRINT",EDGE,{"derivedFrom":subQ0}),-1.0]])]});}
            var Q55;
            {var subQ0=sQuery(id+"F0.wireOp",EDGE,"E22");Q55=makeQuery(id+"F0.imprint","IMPRINT",FACE,{"disambiguationData":[TD([[makeQuery(id+"F0.imprint","IMPRINT",EDGE,{"derivedFrom":subQ0}),-1.0]])]});}
            var Q56;
            {var subQ0=sQuery(id+"F0.wireOp",EDGE,"E25.1.0");Q56=makeQuery(id+"F0.imprint","IMPRINT",FACE,{"disambiguationData":[TD([[makeQuery(id+"F0.imprint","IMPRINT",EDGE,{"derivedFrom":subQ0}),-1.0]])]});}
            var Q57;
            {var subQ0=sQuery(id+"F0.wireOp",EDGE,"E25.2.0");Q57=makeQuery(id+"F0.imprint","IMPRINT",FACE,{"disambiguationData":[TD([[makeQuery(id+"F0.imprint","IMPRINT",EDGE,{"derivedFrom":subQ0}),-1.0]])]});}
            var Q58;
            {var subQ0=sQuery(id+"F0.wireOp",EDGE,"E25.3.0");Q58=makeQuery(id+"F0.imprint","IMPRINT",FACE,{"disambiguationData":[TD([[makeQuery(id+"F0.imprint","IMPRINT",EDGE,{"derivedFrom":subQ0}),-1.0]])]});}
            var Q59;
            {var subQ0=sQuery(id+"F0.wireOp",EDGE,"E25.4.0");Q59=makeQuery(id+"F0.imprint","IMPRINT",FACE,{"disambiguationData":[TD([[makeQuery(id+"F0.imprint","IMPRINT",EDGE,{"derivedFrom":subQ0}),-1.0]])]});}
            var Q60;
            {var subQ0=sQuery(id+"F0.wireOp",EDGE,"E25.5.0");Q60=makeQuery(id+"F0.imprint","IMPRINT",FACE,{"disambiguationData":[TD([[makeQuery(id+"F0.imprint","IMPRINT",EDGE,{"derivedFrom":subQ0}),-1.0]])]});}
            var Q61;
            {var subQ0=sQuery(id+"F0.wireOp",EDGE,"E25.6.0");Q61=makeQuery(id+"F0.imprint","IMPRINT",FACE,{"disambiguationData":[TD([[makeQuery(id+"F0.imprint","IMPRINT",EDGE,{"derivedFrom":subQ0}),-1.0]])]});}
            var Q62;
            {var subQ0=sQuery(id+"F0.wireOp",EDGE,"E25.7.0");Q62=makeQuery(id+"F0.imprint","IMPRINT",FACE,{"disambiguationData":[TD([[makeQuery(id+"F0.imprint","IMPRINT",EDGE,{"derivedFrom":subQ0}),-1.0]])]});}
            extrude(context, id + "F1", {"entities" : qUnion([Q0, Q1, Q2, Q3, Q4, Q5, Q6, Q7, Q8, Q9, Q10, Q11, Q12, Q13, Q14, Q15, Q16, Q17, Q18, Q19, Q20, Q21, Q22, Q23, Q24, Q25, Q26, Q27, Q28, Q29, Q30, Q31, Q32, Q33, Q34, Q35, Q36, Q37, Q38, Q39, Q40, Q41, Q42, Q43, Q44, Q45, Q46, Q47, Q48, Q49, Q50, Q51, Q52, Q53, Q54, Q55, Q56, Q57, Q58, Q59, Q60, Q61, Q62]), "depth" : 3.8 * mm});
        }
    });
